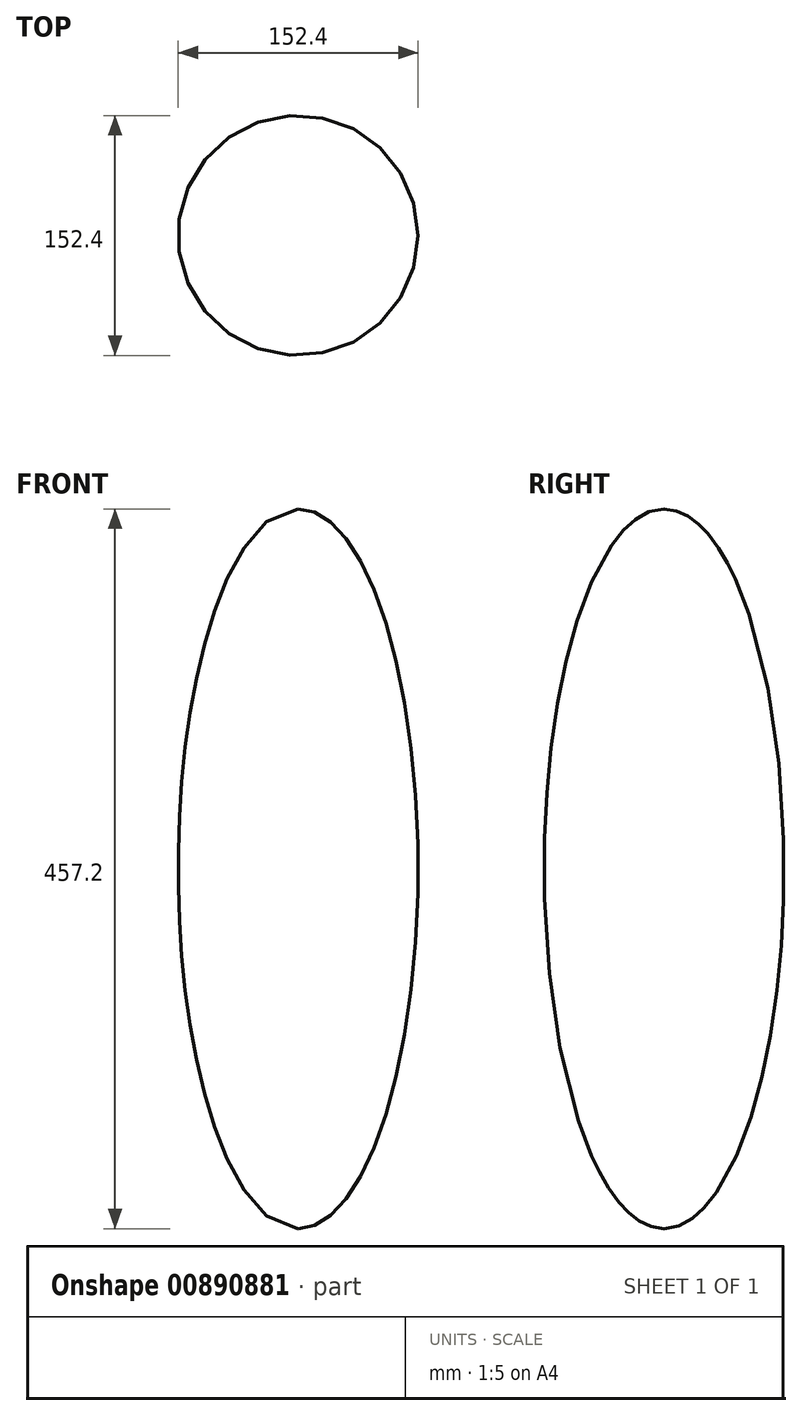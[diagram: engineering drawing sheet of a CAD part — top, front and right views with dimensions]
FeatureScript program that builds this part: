
annotation { "Feature Type Name" : "Feature", "Feature Type Description" : "" }
export const myFeature = defineFeature(function(context is Context, id is Id, definition is map)
    precondition{}
    {
        {
            var Q0;
            Q0=qCreatedBy(makeId("Front.planeOp"),FACE);
            var sketch = newSketch(context, id + "F0", { "sketchPlane" : qUnion([Q0])});
            skEllipse(sketch, "E0", {"center": v(0, 0) * mm, "majorRadius": 228.6 * mm, "minorRadius": 76.2 * mm, "majorAxis": v(0, 1)});
            skLineSegment(sketch, "E1", {"start": v(0, 228.6) * mm, "end": v(0, -228.6) * mm});
            skLineSegment(sketch, "E2", {"start": v(-76.2, 0) * mm, "end": v(76.2, 0) * mm});
            skSolve(sketch);
        }
        {
            var Q0;
            {var subQ0=sQuery(id+"F0.wireOp",EDGE,"E1");Q0=makeQuery(id+"F0.imprint","IMPRINT",FACE,{"disambiguationData":[TD([[makeQuery(id+"F0.imprint","IMPRINT",EDGE,{"derivedFrom":subQ0}),1.0]])]});}
            var Q1;
            Q1=sQuery(id+"F0.wireOp",EDGE,"E1");
            revolve(context, id + "F1", {"surfaceOperationType" : NewSurfaceOperationType.NEW, "entities" : qUnion([Q0]), "axis" : qUnion([Q1]), "revolveType" : RevolveType.FULL});
        }
    });
